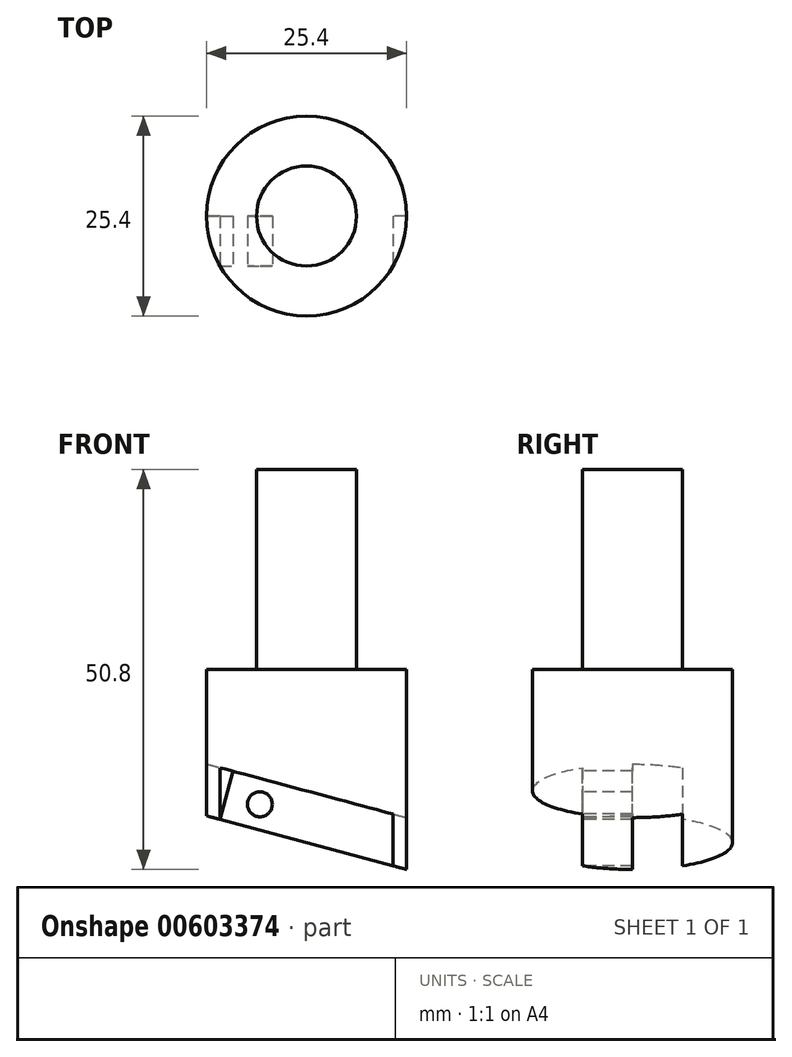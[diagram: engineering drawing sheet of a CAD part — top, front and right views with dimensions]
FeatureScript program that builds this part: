
annotation { "Feature Type Name" : "Feature", "Feature Type Description" : "" }
export const myFeature = defineFeature(function(context is Context, id is Id, definition is map)
    precondition{}
    {
        {
            var Q0;
            Q0=qCreatedBy(makeId("Front.planeOp"),FACE);
            var sketch = newSketch(context, id + "F0", { "sketchPlane" : qUnion([Q0])});
            skLineSegment(sketch, "E0", {"start": v(6.35, 9.48) * mm, "end": v(12.7, 9.48) * mm});
            skLineSegment(sketch, "E1", {"start": v(12.7, 9.48) * mm, "end": v(12.7, -15.92) * mm});
            skLineSegment(sketch, "E2", {"start": v(12.7, -15.92) * mm, "end": v(0, -15.92) * mm});
            skLineSegment(sketch, "E3", {"start": v(0, -15.92) * mm, "end": v(0, 34.88) * mm});
            skLineSegment(sketch, "E4", {"start": v(0, 34.88) * mm, "end": v(6.35, 34.88) * mm});
            skLineSegment(sketch, "E5", {"start": v(6.35, 34.88) * mm, "end": v(6.35, 9.48) * mm});
            skLineSegment(sketch, "E6", {"start": v(12.7, -15.92) * mm, "end": v(-12.7, -9.11) * mm});
            skLineSegment(sketch, "E7", {"start": v(0, -15.92) * mm, "end": v(-12.7, -15.92) * mm});
            skLineSegment(sketch, "E8", {"start": v(-12.7, -15.92) * mm, "end": v(-12.7, -9.11) * mm});
            skLineSegment(sketch, "E9", {"start": v(-12.7, -2.54) * mm, "end": v(12.7, -9.35) * mm});
            skLineSegment(sketch, "E10", {"start": v(-12.7, -9.11) * mm, "end": v(-11.06, -2.98) * mm});
            skLineSegment(sketch, "E11", {"start": v(-12.7, -9.11) * mm, "end": v(-12.7, -2.54) * mm});
            skPoint(sketch, "E12.orphan", {"position": v(-12.7, 0) * mm});
            skSolve(sketch);
        }
        {
            var Q0;
            Q0=makeQuery(id+"F0.imprint","IMPRINT",FACE,{"disambiguationData":[TD([[makeQuery(id+"F0.imprint","IMPRINT",EDGE,{"derivedFrom":sQuery(id+"F0.wireOp",EDGE,"E0")}),-1.0]])]});
            var Q1;
            {var subQ0=sQuery(id+"F0.wireOp",EDGE,"E2");Q1=makeQuery(id+"F0.imprint","IMPRINT",FACE,{"disambiguationData":[TD([[makeQuery(id+"F0.imprint","IMPRINT",EDGE,{"derivedFrom":subQ0}),-1.0]])]});}
            var Q2;
            {var subQ3=sQuery(id+"F0.wireOp",EDGE,"E9");var subQ5=sQuery(id+"F0.wireOp",EDGE,"E3");var subQ6=makeQuery(id+"F0.imprint","INTERSECT",VERTEX,{"derivedFrom":[subQ5,subQ3]});Q2=makeQuery(id+"F0.imprint","IMPRINT",FACE,{"disambiguationData":[TD([[makeQuery(id+"F0.imprint","IMPRINT",EDGE,{"disambiguationData":[TD([[subQ6,1.0]])],"derivedFrom":subQ5}),-1.0]])]});}
            var Q3;
            Q3=sQuery(id+"F0.wireOp",EDGE,"E3");
            revolve(context, id + "F1", {"entities" : qUnion([Q0, Q1, Q2]), "axis" : qUnion([Q3]), "revolveType" : RevolveType.FULL});
        }
        {
            var Q0;
            {var subQ0=sQuery(id+"F0.wireOp",EDGE,"E7");Q0=makeQuery(id+"F0.imprint","IMPRINT",FACE,{"disambiguationData":[TD([[makeQuery(id+"F0.imprint","IMPRINT",EDGE,{"derivedFrom":subQ0}),-1.0]])]});}
            var Q1;
            {var subQ0=sQuery(id+"F0.wireOp",EDGE,"E2");Q1=makeQuery(id+"F0.imprint","IMPRINT",FACE,{"disambiguationData":[TD([[makeQuery(id+"F0.imprint","IMPRINT",EDGE,{"derivedFrom":subQ0}),-1.0]])]});}
            extrude(context, id + "F2", {"entities" : qUnion([Q0, Q1]), "operationType" : NewBodyOperationType.REMOVE, "endBound" : BoundingType.SYMMETRIC, "oppositeDirection" : true, "depth" : 25.4 * mm, "offsetDistance" : 25.4 * mm});
        }
        {
            var Q0;
            {var subQ5=sQuery(id+"F0.wireOp",EDGE,"E10");Q0=makeQuery(id+"F0.imprint","IMPRINT",FACE,{"disambiguationData":[TD([[makeQuery(id+"F0.imprint","IMPRINT",EDGE,{"derivedFrom":subQ5}),-1.0]])]});}
            var Q1;
            {var subQ3=sQuery(id+"F0.wireOp",EDGE,"E9");var subQ5=sQuery(id+"F0.wireOp",EDGE,"E3");var subQ6=makeQuery(id+"F0.imprint","INTERSECT",VERTEX,{"derivedFrom":[subQ5,subQ3]});Q1=makeQuery(id+"F0.imprint","IMPRINT",FACE,{"disambiguationData":[TD([[makeQuery(id+"F0.imprint","IMPRINT",EDGE,{"disambiguationData":[TD([[subQ6,1.0]])],"derivedFrom":subQ5}),-1.0]])]});}
            var Q2;
            {var subQ2=sQuery(id+"F0.wireOp",EDGE,"E10");Q2=makeQuery(id+"F0.imprint","IMPRINT",FACE,{"disambiguationData":[TD([[makeQuery(id+"F0.imprint","IMPRINT",EDGE,{"derivedFrom":subQ2}),1.0]])]});}
            extrude(context, id + "F3", {"entities" : qUnion([Q0, Q1, Q2]), "operationType" : NewBodyOperationType.REMOVE, "oppositeDirection" : true, "depth" : 6.35 * mm, "offsetDistance" : 25.4 * mm});
        }
        {
            var Q0;
            {var subQ0=sQuery(id+"F0.wireOp",EDGE,"E1");var subQ1=sQuery(id+"F0.wireOp",EDGE,"E6");Q0=makeQuery(id+"F3.boolean.opBoolean","SPLIT",FACE,{"disambiguationData":[TD([makeQuery(id+"F3.opExtrude","CAP_FACE",FACE,{"disambiguationData":[OSD([subQ0,subQ1,sQuery(id+"F0.wireOp",EDGE,"E9"),sQuery(id+"F0.wireOp",EDGE,"E11")])],"isStart":true})])],"derivedFrom":makeQuery(id+"F2.boolean.opBoolean","COPY",FACE,{"derivedFrom":makeQuery(id+"F2.opExtrude","SWEPT_FACE",FACE,{"disambiguationData":[OSD([subQ1])]})})});}
            var sketch = newSketch(context, id + "F4", { "sketchPlane" : qUnion([Q0])});
            skLineSegment(sketch, "E13", {"start": v(3.59, 0) * mm, "end": v(3.59, 6.35) * mm});
            skLineSegment(sketch, "E14", {"start": v(14.63, 6.35) * mm, "end": v(-8.15, 6.35) * mm});
            skLineSegment(sketch, "E15", {"start": v(-8.15, 6.35) * mm, "end": v(-8.15, 12.7) * mm});
            skLineSegment(sketch, "E16", {"start": v(14.63, 6.35) * mm, "end": v(14.63, 12.7) * mm});
            skLineSegment(sketch, "E17", {"start": v(14.63, 12.7) * mm, "end": v(-8.15, 12.7) * mm});
            skLineSegment(sketch, "E18", {"start": v(-9.9, 0) * mm, "end": v(-9.9, 12.7) * mm});
            skLineSegment(sketch, "E19", {"start": v(-9.9, 12.7) * mm, "end": v(-8.15, 12.7) * mm});
            skLineSegment(sketch, "E20", {"start": v(-8.15, 6.35) * mm, "end": v(-9.9, 6.35) * mm});
            skSolve(sketch);
        }
        {
            var Q0;
            {var subQ0=sQuery(id+"F4.wireOp",EDGE,"E14");var subQ1=makeQuery(id+"F4.imprint","INTERSECT",VERTEX,{"derivedFrom":[sQuery(id+"F4.wireOp",EDGE,"E13"),subQ0]});Q0=makeQuery(id+"F4.imprint","IMPRINT",FACE,{"disambiguationData":[TD([[makeQuery(id+"F4.imprint","IMPRINT",EDGE,{"disambiguationData":[TD([[subQ1,1.0]])],"derivedFrom":subQ0}),-1.0]])]});}
            var Q1;
            {var subQ0=sQuery(id+"F4.wireOp",EDGE,"E15");Q1=makeQuery(id+"F4.imprint","IMPRINT",FACE,{"disambiguationData":[TD([[makeQuery(id+"F4.imprint","IMPRINT",EDGE,{"derivedFrom":subQ0}),-1.0]])]});}
            var Q2;
            Q2=makeQuery(id+"F4.imprint","IMPRINT",FACE,{"disambiguationData":[TD([[makeQuery(id+"F4.imprint","IMPRINT",EDGE,{"derivedFrom":sQuery(id+"F4.wireOp",EDGE,"E15")}),1.0]])]});
            extrude(context, id + "F5", {"entities" : qUnion([Q0, Q1, Q2]), "operationType" : NewBodyOperationType.REMOVE, "oppositeDirection" : true, "depth" : 6.35 * mm, "offsetDistance" : 25.4 * mm});
        }
        {
            var Q0;
            Q0=makeQuery(id+"F5.boolean.opBoolean","COPY",FACE,{"derivedFrom":makeQuery(id+"F5.opExtrude","SWEPT_FACE",FACE,{"disambiguationData":[OSD([sQuery(id+"F4.wireOp",EDGE,"E14"),sQuery(id+"F4.wireOp",EDGE,"E20")])]})});
            var sketch = newSketch(context, id + "F6", { "sketchPlane" : qUnion([Q0])});
            skLineSegment(sketch, "E21", {"start": v(-11, -9.57) * mm, "end": v(-9.36, -3.44) * mm});
            skLineSegment(sketch, "E22", {"start": v(-10.18, -6.5) * mm, "end": v(11, -12.18) * mm});
            skCircle(sketch, "E23", {"center": v(-5.93, -7.64) * mm, "radius": 1.59 * mm});
            skCircle(sketch, "E24", {"center": v(7.93, -11.36) * mm, "radius": 1.59 * mm});
            skSolve(sketch);
        }
        {
            var Q0;
            {var subQ0=sQuery(id+"F6.wireOp",EDGE,"E23");var subQ1=sQuery(id+"F6.wireOp",EDGE,"E22");var subQ2=makeQuery(id+"F6.imprint","INTERSECT",VERTEX,{"disambiguationData":[OD(0.0)],"derivedFrom":[subQ1,subQ0]});Q0=makeQuery(id+"F6.imprint","IMPRINT",FACE,{"disambiguationData":[TD([[makeQuery(id+"F6.imprint","IMPRINT",EDGE,{"disambiguationData":[TD([[subQ2,-1.0]])],"derivedFrom":subQ1}),-1.0]])]});}
            var Q1;
            {var subQ0=sQuery(id+"F6.wireOp",EDGE,"E23");var subQ1=sQuery(id+"F6.wireOp",EDGE,"E22");var subQ2=makeQuery(id+"F6.imprint","INTERSECT",VERTEX,{"disambiguationData":[OD(0.0)],"derivedFrom":[subQ1,subQ0]});Q1=makeQuery(id+"F6.imprint","IMPRINT",FACE,{"disambiguationData":[TD([[makeQuery(id+"F6.imprint","IMPRINT",EDGE,{"disambiguationData":[TD([[subQ2,-1.0]])],"derivedFrom":subQ1}),1.0]])]});}
            var Q2;
            {var subQ0=sQuery(id+"F6.wireOp",EDGE,"E24");var subQ1=sQuery(id+"F6.wireOp",EDGE,"E22");var subQ2=makeQuery(id+"F6.imprint","INTERSECT",VERTEX,{"disambiguationData":[OD(0.0)],"derivedFrom":[subQ1,subQ0]});Q2=makeQuery(id+"F6.imprint","IMPRINT",FACE,{"disambiguationData":[TD([[makeQuery(id+"F6.imprint","IMPRINT",EDGE,{"disambiguationData":[TD([[subQ2,-1.0]])],"derivedFrom":subQ1}),1.0]])]});}
            var Q3;
            {var subQ0=sQuery(id+"F6.wireOp",EDGE,"E24");var subQ1=sQuery(id+"F6.wireOp",EDGE,"E22");var subQ2=makeQuery(id+"F6.imprint","INTERSECT",VERTEX,{"disambiguationData":[OD(0.0)],"derivedFrom":[subQ1,subQ0]});Q3=makeQuery(id+"F6.imprint","IMPRINT",FACE,{"disambiguationData":[TD([[makeQuery(id+"F6.imprint","IMPRINT",EDGE,{"disambiguationData":[TD([[subQ2,-1.0]])],"derivedFrom":subQ1}),-1.0]])]});}
            var Q4;
            Q4=sQuery(id+"F6.wireOp",EDGE,"E23");
            var Q5;
            Q5=sQuery(id+"F6.wireOp",EDGE,"E24");
            extrude(context, id + "F7", {"entities" : qUnion([Q0, Q1, Q2, Q3]), "operationType" : NewBodyOperationType.REMOVE, "surfaceEntities" : qUnion([Q4, Q5]), "oppositeDirection" : true, "depth" : 6.35 * mm, "offsetDistance" : 25.4 * mm});
        }
    });
